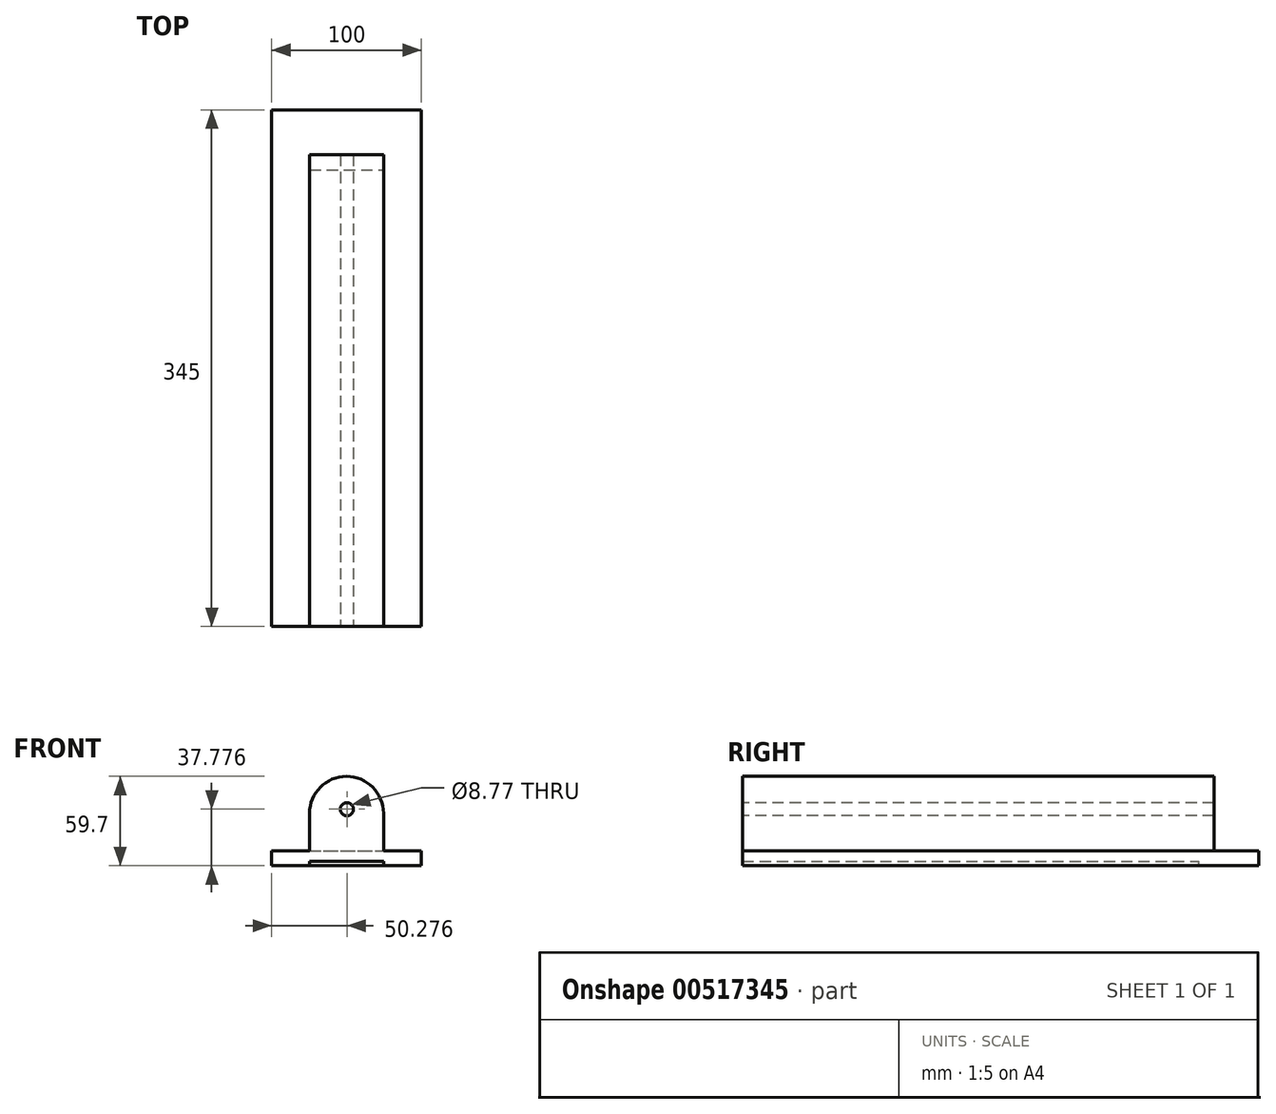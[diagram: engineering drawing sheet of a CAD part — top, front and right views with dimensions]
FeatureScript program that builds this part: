
annotation { "Feature Type Name" : "Feature", "Feature Type Description" : "" }
export const myFeature = defineFeature(function(context is Context, id is Id, definition is map)
    precondition{}
    {
        {
            var Q0;
            Q0=qCreatedBy(makeId("Top.planeOp"),FACE);
            var sketch = newSketch(context, id + "F0", { "sketchPlane" : qUnion([Q0])});
            skLineSegment(sketch, "E0.bottom", {"start": v(0, 0) * mm, "end": v(100, 0) * mm});
            skLineSegment(sketch, "E0.top", {"start": v(0, 40) * mm, "end": v(100, 40) * mm});
            skLineSegment(sketch, "E0.left", {"start": v(0, 0) * mm, "end": v(0, 40) * mm});
            skLineSegment(sketch, "E0.right", {"start": v(100, 0) * mm, "end": v(100, 40) * mm});
            skSolve(sketch);
        }
        {
            var Q0;
            Q0 = qSketchRegion(id + "F0", true);
            extrude(context, id + "F1", {"entities" : qUnion([Q0]), "depth" : 10 * mm, "offsetDistance" : 25 * mm});
        }
        {
            var Q0;
            Q0=makeQuery(id+"F1.opExtrude","SWEPT_FACE",FACE,{"disambiguationData":[OSD([sQuery(id+"F0.wireOp",EDGE,"E0.bottom")])]});
            var sketch = newSketch(context, id + "F2", { "sketchPlane" : qUnion([Q0])});
            skLineSegment(sketch, "E1", {"start": v(25.3, 0) * mm, "end": v(25.3, 35) * mm});
            skArc(sketch, "E2", {"start": v(25.3, 35) * mm, "mid": v(50, 59.7) * mm, "end": v(74.7, 35) * mm});
            skLineSegment(sketch, "E3", {"start": v(74.7, 35) * mm, "end": v(74.7, 0) * mm});
            skLineSegment(sketch, "E4", {"start": v(74.7, 0) * mm, "end": v(25.3, 0) * mm});
            skSolve(sketch);
        }
        {
            var Q0;
            Q0 = qSketchRegion(id + "F2", true);
            extrude(context, id + "F3", {"entities" : qUnion([Q0]), "operationType" : NewBodyOperationType.ADD, "oppositeDirection" : true, "depth" : 10 * mm, "offsetDistance" : 25 * mm});
        }
        {
            var Q0;
            Q0=makeQuery(id+"F3.boolean.opBoolean","MERGE",FACE,{"derivedFrom":[makeQuery(id+"F1.opExtrude","SWEPT_FACE",FACE,{"disambiguationData":[OSD([sQuery(id+"F0.wireOp",EDGE,"E0.bottom")])]}),makeQuery(id+"F3.opExtrude","CAP_FACE",FACE,{"disambiguationData":[OSD([sQuery(id+"F2.wireOp",EDGE,"E1"),sQuery(id+"F2.wireOp",EDGE,"E2"),sQuery(id+"F2.wireOp",EDGE,"E3"),sQuery(id+"F2.wireOp",EDGE,"E4")])],"isStart":true})]});
            var sketch = newSketch(context, id + "F4", { "sketchPlane" : qUnion([Q0])});
            skLineSegment(sketch, "E5.bottom", {"start": v(25.3, 0) * mm, "end": v(74.7, 0) * mm});
            skLineSegment(sketch, "E5.top", {"start": v(25.3, 3) * mm, "end": v(74.7, 3) * mm});
            skLineSegment(sketch, "E5.left", {"start": v(25.3, 0) * mm, "end": v(25.3, 3) * mm});
            skLineSegment(sketch, "E5.right", {"start": v(74.7, 0) * mm, "end": v(74.7, 3) * mm});
            skSolve(sketch);
        }
        {
            var Q0;
            Q0=makeQuery(id+"F4.imprint","IMPRINT",FACE,{"disambiguationData":[TD([[makeQuery(id+"F4.imprint","IMPRINT",EDGE,{"derivedFrom":sQuery(id+"F4.wireOp",EDGE,"E5.top")}),1.0]])]});
            extrude(context, id + "F5", {"entities" : qUnion([Q0]), "operationType" : NewBodyOperationType.ADD, "depth" : 305 * mm, "offsetDistance" : 25 * mm});
        }
        {
            var Q0;
            Q0=makeQuery(id+"F5.opExtrude","CAP_FACE",FACE,{"disambiguationData":[OSD([sQuery(id+"F0.wireOp",EDGE,"E0.bottom"),sQuery(id+"F0.wireOp",EDGE,"E0.left"),sQuery(id+"F0.wireOp",EDGE,"E0.right"),sQuery(id+"F2.wireOp",EDGE,"E1"),sQuery(id+"F2.wireOp",EDGE,"E2"),sQuery(id+"F2.wireOp",EDGE,"E3"),sQuery(id+"F4.wireOp",EDGE,"E5.top"),sQuery(id+"F4.wireOp",EDGE,"E5.left"),sQuery(id+"F4.wireOp",EDGE,"E5.right")])],"isStart":false});
            var sketch = newSketch(context, id + "F6", { "sketchPlane" : qUnion([Q0])});
            skCircle(sketch, "E6", {"center": v(50.28, 37.78) * mm, "radius": 4.38 * mm});
            skSolve(sketch);
        }
        {
            var Q0;
            Q0 = qSketchRegion(id + "F6", true);
            extrude(context, id + "F7", {"entities" : qUnion([Q0]), "operationType" : NewBodyOperationType.REMOVE, "endBound" : BoundingType.THROUGH_ALL, "oppositeDirection" : true, "depth" : 25 * mm, "offsetDistance" : 25 * mm});
        }
    });
